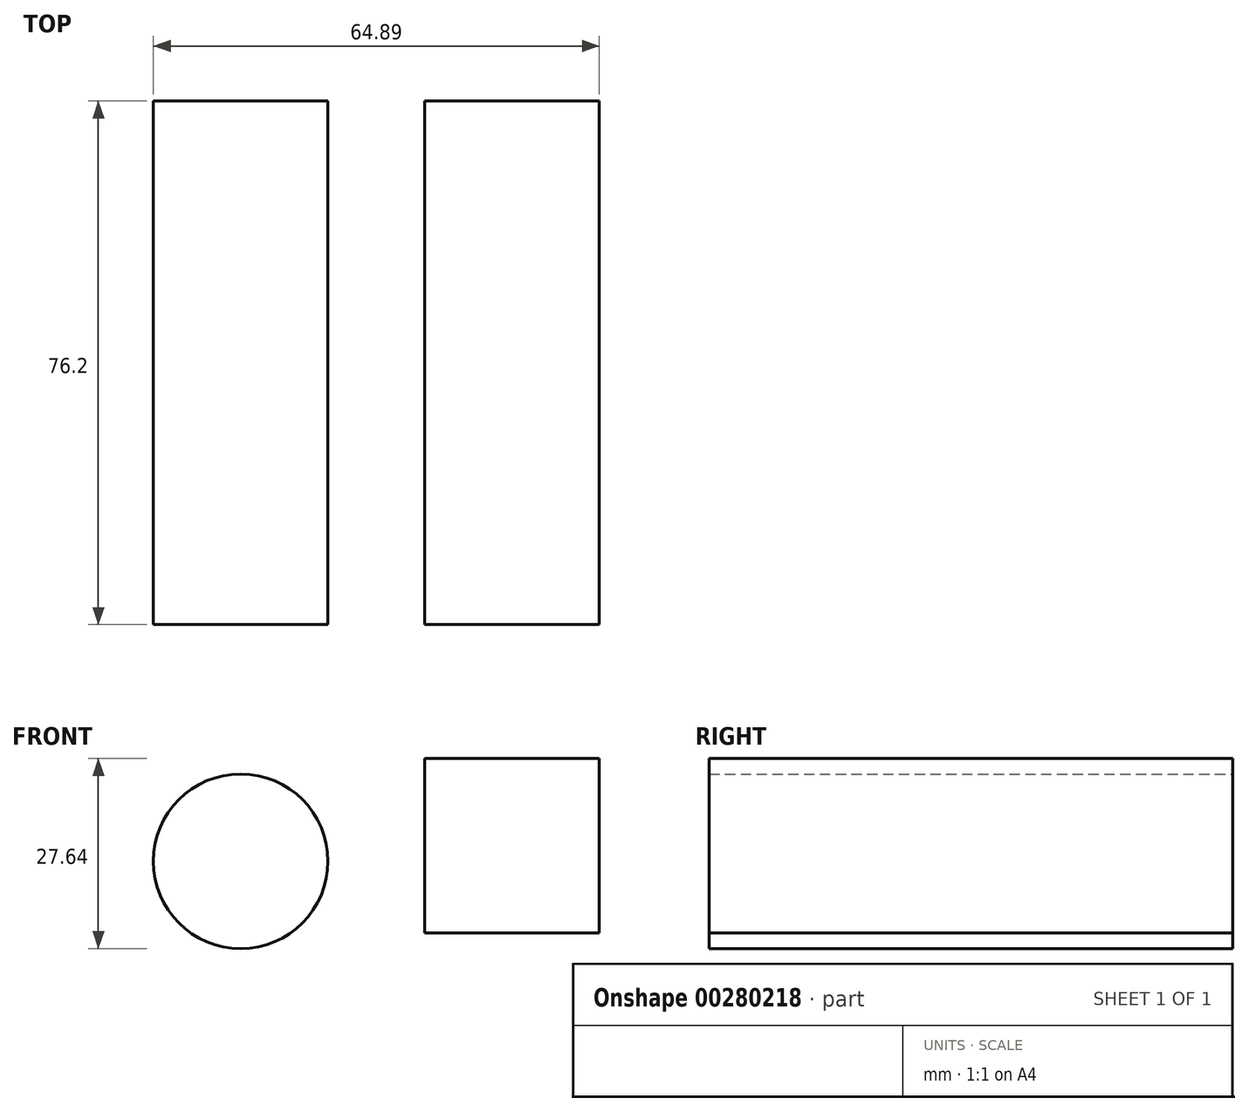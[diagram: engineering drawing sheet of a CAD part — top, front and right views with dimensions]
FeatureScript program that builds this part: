
annotation { "Feature Type Name" : "Feature", "Feature Type Description" : "" }
export const myFeature = defineFeature(function(context is Context, id is Id, definition is map)
    precondition{}
    {
        {
            var Q0;
            Q0=qCreatedBy(makeId("Front.planeOp"),FACE);
            var sketch = newSketch(context, id + "F0", { "sketchPlane" : qUnion([Q0])});
            skCircle(sketch, "E0", {"center": v(-52.19, 51) * mm, "radius": 12.7 * mm});
            skLineSegment(sketch, "E1.bottom", {"start": v(-25.4, 71.47) * mm, "end": v(0, 71.47) * mm});
            skLineSegment(sketch, "E1.top", {"start": v(-25.4, 46.07) * mm, "end": v(0, 46.07) * mm});
            skLineSegment(sketch, "E1.left", {"start": v(-25.4, 71.47) * mm, "end": v(-25.4, 46.07) * mm});
            skLineSegment(sketch, "E1.right", {"start": v(0, 71.47) * mm, "end": v(0, 46.07) * mm});
            skSolve(sketch);
        }
        {
            var Q0;
            Q0=makeQuery(id+"F0.imprint","IMPRINT",FACE,{"disambiguationData":[TD([[makeQuery(id+"F0.imprint","IMPRINT",EDGE,{"derivedFrom":sQuery(id+"F0.wireOp",EDGE,"E0")}),1.0]])]});
            extrude(context, id + "F1", {"entities" : qUnion([Q0]), "depth" : 76.2 * mm});
        }
        {
            var Q0;
            Q0=qCreatedBy(makeId("Front.planeOp"),FACE);
            var sketch = newSketch(context, id + "F2", { "sketchPlane" : qUnion([Q0])});
            skLineSegment(sketch, "E2.bottom", {"start": v(-25.4, 65.95) * mm, "end": v(0, 65.95) * mm});
            skLineSegment(sketch, "E2.top", {"start": v(-25.4, 40.55) * mm, "end": v(0, 40.55) * mm});
            skLineSegment(sketch, "E2.left", {"start": v(-25.4, 65.95) * mm, "end": v(-25.4, 40.55) * mm});
            skLineSegment(sketch, "E2.right", {"start": v(0, 65.95) * mm, "end": v(0, 40.55) * mm});
            skSolve(sketch);
        }
        {
            var Q0;
            Q0=makeQuery(id+"F2.imprint","IMPRINT",FACE,{"disambiguationData":[TD([[makeQuery(id+"F2.imprint","IMPRINT",EDGE,{"derivedFrom":sQuery(id+"F2.wireOp",EDGE,"E2.bottom")}),-1.0]])]});
            extrude(context, id + "F3", {"entities" : qUnion([Q0]), "depth" : 76.2 * mm});
        }
    });
